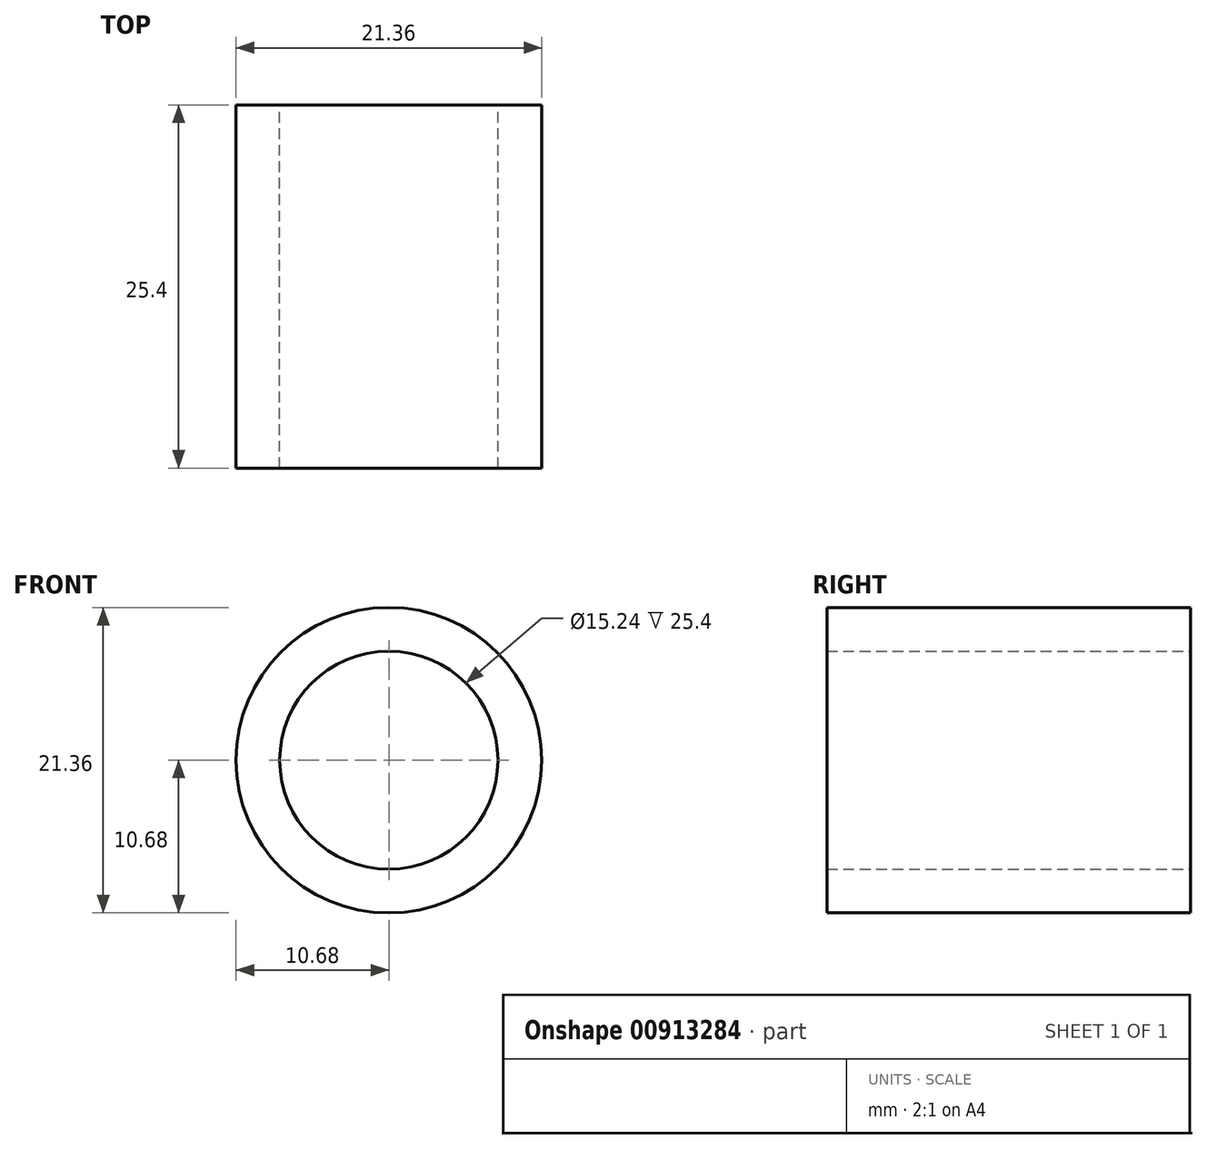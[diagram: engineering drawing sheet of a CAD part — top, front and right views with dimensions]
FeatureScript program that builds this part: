
annotation { "Feature Type Name" : "Feature", "Feature Type Description" : "" }
export const myFeature = defineFeature(function(context is Context, id is Id, definition is map)
    precondition{}
    {
        {
            var Q0;
            Q0=qCreatedBy(makeId("Front.planeOp"),FACE);
            var sketch = newSketch(context, id + "F0", { "sketchPlane" : qUnion([Q0])});
            skCircle(sketch, "E0", {"center": v(0, 0) * mm, "radius": 10.68 * mm});
            skCircle(sketch, "E1", {"center": v(0, 0) * mm, "radius": 7.62 * mm});
            skSolve(sketch);
        }
        {
            var Q0;
            Q0=makeQuery(id+"F0.imprint","IMPRINT",FACE,{"disambiguationData":[TD([[makeQuery(id+"F0.imprint","IMPRINT",EDGE,{"derivedFrom":sQuery(id+"F0.wireOp",EDGE,"E0")}),1.0]])]});
            extrude(context, id + "F1", {"entities" : qUnion([Q0]), "depth" : 25.4 * mm, "offsetDistance" : 25.4 * mm});
        }
    });
